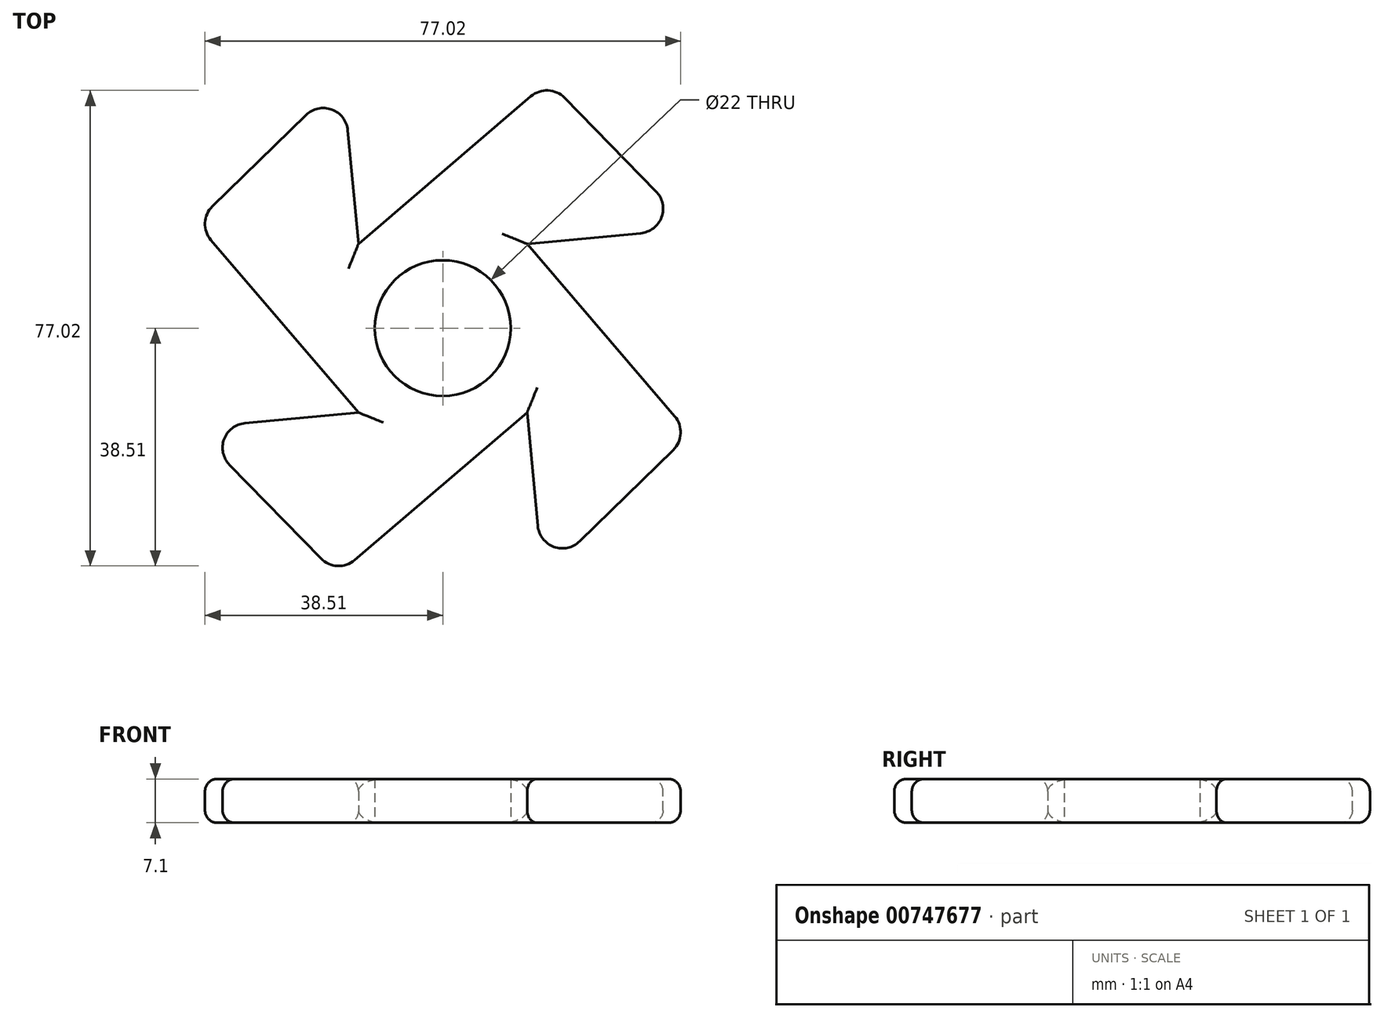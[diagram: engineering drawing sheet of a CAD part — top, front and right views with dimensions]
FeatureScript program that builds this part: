
annotation { "Feature Type Name" : "Feature", "Feature Type Description" : "" }
export const myFeature = defineFeature(function(context is Context, id is Id, definition is map)
    precondition{}
    {
        {
            var Q0;
            Q0=qCreatedBy(makeId("Top.planeOp"),FACE);
            var sketch = newSketch(context, id + "F0", { "sketchPlane" : qUnion([Q0])});
            skCircle(sketch, "E0", {"center": v(0, 0) * mm, "radius": 11 * mm});
            skCircle(sketch, "E1.cCircle", {"center": v(0, 0) * mm, "radius": 40.18 * mm, "construction": true});
            skLineSegment(sketch, "E1.0", {"start": v(39.98, -17.12) * mm, "end": v(16.17, -40.38) * mm});
            skLineSegment(sketch, "E1.1", {"start": v(16.17, -40.38) * mm, "end": v(-17.12, -39.98) * mm});
            skLineSegment(sketch, "E1.2", {"start": v(-17.12, -39.98) * mm, "end": v(-40.38, -16.17) * mm});
            skLineSegment(sketch, "E1.3", {"start": v(-40.38, -16.17) * mm, "end": v(-39.98, 17.12) * mm});
            skLineSegment(sketch, "E1.4", {"start": v(-39.98, 17.12) * mm, "end": v(-16.17, 40.38) * mm});
            skLineSegment(sketch, "E1.5", {"start": v(-16.17, 40.38) * mm, "end": v(17.12, 39.98) * mm});
            skLineSegment(sketch, "E1.6", {"start": v(17.12, 39.98) * mm, "end": v(40.38, 16.17) * mm});
            skLineSegment(sketch, "E1.7", {"start": v(40.38, 16.17) * mm, "end": v(39.98, -17.12) * mm});
            skPoint(sketch, "E1.0.midPoint", {"position": v(28.08, -28.75) * mm});
            skCircle(sketch, "E2.cCircle", {"center": v(0, 0) * mm, "radius": 13.65 * mm, "construction": true});
            skLineSegment(sketch, "E2.0", {"start": v(13.65, -13.65) * mm, "end": v(-13.65, -13.65) * mm});
            skLineSegment(sketch, "E2.1", {"start": v(-13.65, -13.65) * mm, "end": v(-13.65, 13.65) * mm});
            skLineSegment(sketch, "E2.2", {"start": v(-13.65, 13.65) * mm, "end": v(13.65, 13.65) * mm});
            skLineSegment(sketch, "E2.3", {"start": v(13.65, 13.65) * mm, "end": v(13.65, -13.65) * mm});
            skPoint(sketch, "E2.0.midPoint", {"position": v(0, -13.65) * mm});
            skLineSegment(sketch, "E3", {"start": v(-13.65, 13.65) * mm, "end": v(-16.17, 40.38) * mm});
            skLineSegment(sketch, "E4", {"start": v(-13.65, 13.65) * mm, "end": v(17.12, 39.98) * mm});
            skLineSegment(sketch, "E5", {"start": v(13.65, 13.65) * mm, "end": v(40.38, 16.17) * mm});
            skLineSegment(sketch, "E6", {"start": v(13.65, 13.65) * mm, "end": v(39.98, -17.12) * mm});
            skLineSegment(sketch, "E7", {"start": v(13.65, -13.65) * mm, "end": v(16.17, -40.38) * mm});
            skLineSegment(sketch, "E8", {"start": v(13.65, -13.65) * mm, "end": v(-17.12, -39.98) * mm});
            skLineSegment(sketch, "E9", {"start": v(-13.65, -13.65) * mm, "end": v(-40.38, -16.17) * mm});
            skLineSegment(sketch, "E10", {"start": v(-13.65, -13.65) * mm, "end": v(-39.98, 17.12) * mm});
            skSolve(sketch);
        }
        {
            var Q0;
            Q0=makeQuery(id+"F0.imprint","IMPRINT",FACE,{"disambiguationData":[TD([[makeQuery(id+"F0.imprint","IMPRINT",EDGE,{"derivedFrom":sQuery(id+"F0.wireOp",EDGE,"E0")}),-1.0]])]});
            var Q1;
            Q1=makeQuery(id+"F0.imprint","IMPRINT",FACE,{"disambiguationData":[TD([[makeQuery(id+"F0.imprint","IMPRINT",EDGE,{"derivedFrom":sQuery(id+"F0.wireOp",EDGE,"E1.6")}),-1.0]])]});
            var Q2;
            Q2=makeQuery(id+"F0.imprint","IMPRINT",FACE,{"disambiguationData":[TD([[makeQuery(id+"F0.imprint","IMPRINT",EDGE,{"derivedFrom":sQuery(id+"F0.wireOp",EDGE,"E1.0")}),-1.0]])]});
            var Q3;
            Q3=makeQuery(id+"F0.imprint","IMPRINT",FACE,{"disambiguationData":[TD([[makeQuery(id+"F0.imprint","IMPRINT",EDGE,{"derivedFrom":sQuery(id+"F0.wireOp",EDGE,"E1.2")}),-1.0]])]});
            var Q4;
            Q4=makeQuery(id+"F0.imprint","IMPRINT",FACE,{"disambiguationData":[TD([[makeQuery(id+"F0.imprint","IMPRINT",EDGE,{"derivedFrom":sQuery(id+"F0.wireOp",EDGE,"E1.4")}),-1.0]])]});
            extrude(context, id + "F1", {"entities" : qUnion([Q0, Q1, Q2, Q3, Q4]), "depth" : 7.1 * mm, "offsetDistance" : 25 * mm});
        }
        {
            var Q0;
            Q0=makeQuery(id+"F1.opExtrude","CAP_EDGE",EDGE,{"disambiguationData":[OSD([sQuery(id+"F0.wireOp",EDGE,"E8")])],"isStart":false});
            var Q1;
            Q1=makeQuery(id+"F1.opExtrude","CAP_EDGE",EDGE,{"disambiguationData":[OSD([sQuery(id+"F0.wireOp",EDGE,"E7")])],"isStart":false});
            var Q2;
            Q2=makeQuery(id+"F1.opExtrude","CAP_EDGE",EDGE,{"disambiguationData":[OSD([sQuery(id+"F0.wireOp",EDGE,"E1.0")])],"isStart":false});
            var Q3;
            Q3=makeQuery(id+"F1.opExtrude","CAP_EDGE",EDGE,{"disambiguationData":[OSD([sQuery(id+"F0.wireOp",EDGE,"E6")])],"isStart":false});
            var Q4;
            Q4=makeQuery(id+"F1.opExtrude","CAP_EDGE",EDGE,{"disambiguationData":[OSD([sQuery(id+"F0.wireOp",EDGE,"E5")])],"isStart":false});
            var Q5;
            Q5=makeQuery(id+"F1.opExtrude","CAP_EDGE",EDGE,{"disambiguationData":[OSD([sQuery(id+"F0.wireOp",EDGE,"E1.6")])],"isStart":false});
            var Q6;
            Q6=makeQuery(id+"F1.opExtrude","CAP_EDGE",EDGE,{"disambiguationData":[OSD([sQuery(id+"F0.wireOp",EDGE,"E4")])],"isStart":false});
            var Q7;
            Q7=makeQuery(id+"F1.opExtrude","CAP_EDGE",EDGE,{"disambiguationData":[OSD([sQuery(id+"F0.wireOp",EDGE,"E3")])],"isStart":false});
            var Q8;
            Q8=makeQuery(id+"F1.opExtrude","CAP_EDGE",EDGE,{"disambiguationData":[OSD([sQuery(id+"F0.wireOp",EDGE,"E1.4")])],"isStart":false});
            var Q9;
            Q9=makeQuery(id+"F1.opExtrude","CAP_EDGE",EDGE,{"disambiguationData":[OSD([sQuery(id+"F0.wireOp",EDGE,"E10")])],"isStart":false});
            var Q10;
            Q10=makeQuery(id+"F1.opExtrude","CAP_EDGE",EDGE,{"disambiguationData":[OSD([sQuery(id+"F0.wireOp",EDGE,"E9")])],"isStart":false});
            var Q11;
            Q11=makeQuery(id+"F1.opExtrude","CAP_EDGE",EDGE,{"disambiguationData":[OSD([sQuery(id+"F0.wireOp",EDGE,"E1.2")])],"isStart":false});
            var Q12;
            Q12=makeQuery(id+"F1.opExtrude","CAP_EDGE",EDGE,{"disambiguationData":[OSD([sQuery(id+"F0.wireOp",EDGE,"E1.2")])],"isStart":true});
            var Q13;
            Q13=makeQuery(id+"F1.opExtrude","CAP_EDGE",EDGE,{"disambiguationData":[OSD([sQuery(id+"F0.wireOp",EDGE,"E9")])],"isStart":true});
            var Q14;
            Q14=makeQuery(id+"F1.opExtrude","CAP_EDGE",EDGE,{"disambiguationData":[OSD([sQuery(id+"F0.wireOp",EDGE,"E10")])],"isStart":true});
            var Q15;
            Q15=makeQuery(id+"F1.opExtrude","CAP_EDGE",EDGE,{"disambiguationData":[OSD([sQuery(id+"F0.wireOp",EDGE,"E1.4")])],"isStart":true});
            var Q16;
            Q16=makeQuery(id+"F1.opExtrude","CAP_EDGE",EDGE,{"disambiguationData":[OSD([sQuery(id+"F0.wireOp",EDGE,"E3")])],"isStart":true});
            var Q17;
            Q17=makeQuery(id+"F1.opExtrude","CAP_EDGE",EDGE,{"disambiguationData":[OSD([sQuery(id+"F0.wireOp",EDGE,"E4")])],"isStart":true});
            var Q18;
            Q18=makeQuery(id+"F1.opExtrude","CAP_EDGE",EDGE,{"disambiguationData":[OSD([sQuery(id+"F0.wireOp",EDGE,"E1.6")])],"isStart":true});
            var Q19;
            Q19=makeQuery(id+"F1.opExtrude","CAP_EDGE",EDGE,{"disambiguationData":[OSD([sQuery(id+"F0.wireOp",EDGE,"E5")])],"isStart":true});
            var Q20;
            Q20=makeQuery(id+"F1.opExtrude","CAP_EDGE",EDGE,{"disambiguationData":[OSD([sQuery(id+"F0.wireOp",EDGE,"E6")])],"isStart":true});
            var Q21;
            Q21=makeQuery(id+"F1.opExtrude","CAP_EDGE",EDGE,{"disambiguationData":[OSD([sQuery(id+"F0.wireOp",EDGE,"E1.0")])],"isStart":true});
            var Q22;
            Q22=makeQuery(id+"F1.opExtrude","CAP_EDGE",EDGE,{"disambiguationData":[OSD([sQuery(id+"F0.wireOp",EDGE,"E7")])],"isStart":true});
            var Q23;
            Q23=makeQuery(id+"F1.opExtrude","CAP_EDGE",EDGE,{"disambiguationData":[OSD([sQuery(id+"F0.wireOp",EDGE,"E8")])],"isStart":true});
            fillet(context, id + "F2", {"entities" : qUnion([Q0, Q1, Q2, Q3, Q4, Q5, Q6, Q7, Q8, Q9, Q10, Q11, Q12, Q13, Q14, Q15, Q16, Q17, Q18, Q19, Q20, Q21, Q22, Q23]), "radius" : 2 * mm, "tangentPropagation" : true, "allowEdgeOverflow" : false});
        }
        {
            var Q0;
            Q0=makeQuery(id+"F1.opExtrude","SWEPT_EDGE",EDGE,{"disambiguationData":[OSD([sQuery(id+"F0.wireOp",EDGE,"E1.0"),sQuery(id+"F0.wireOp",EDGE,"E1.7"),sQuery(id+"F0.wireOp",EDGE,"E6")])]});
            var Q1;
            Q1=makeQuery(id+"F1.opExtrude","SWEPT_EDGE",EDGE,{"disambiguationData":[OSD([sQuery(id+"F0.wireOp",EDGE,"E1.5"),sQuery(id+"F0.wireOp",EDGE,"E1.6"),sQuery(id+"F0.wireOp",EDGE,"E4")])]});
            var Q2;
            Q2=makeQuery(id+"F1.opExtrude","SWEPT_EDGE",EDGE,{"disambiguationData":[OSD([sQuery(id+"F0.wireOp",EDGE,"E1.3"),sQuery(id+"F0.wireOp",EDGE,"E1.4"),sQuery(id+"F0.wireOp",EDGE,"E10")])]});
            var Q3;
            Q3=makeQuery(id+"F1.opExtrude","SWEPT_EDGE",EDGE,{"disambiguationData":[OSD([sQuery(id+"F0.wireOp",EDGE,"E1.1"),sQuery(id+"F0.wireOp",EDGE,"E1.2"),sQuery(id+"F0.wireOp",EDGE,"E8")])]});
            var Q4;
            Q4=makeQuery(id+"F1.opExtrude","SWEPT_EDGE",EDGE,{"disambiguationData":[OSD([sQuery(id+"F0.wireOp",EDGE,"E1.0"),sQuery(id+"F0.wireOp",EDGE,"E1.1"),sQuery(id+"F0.wireOp",EDGE,"E7")])]});
            var Q5;
            Q5=makeQuery(id+"F1.opExtrude","SWEPT_EDGE",EDGE,{"disambiguationData":[OSD([sQuery(id+"F0.wireOp",EDGE,"E1.2"),sQuery(id+"F0.wireOp",EDGE,"E1.3"),sQuery(id+"F0.wireOp",EDGE,"E9")])]});
            var Q6;
            Q6=makeQuery(id+"F1.opExtrude","SWEPT_EDGE",EDGE,{"disambiguationData":[OSD([sQuery(id+"F0.wireOp",EDGE,"E1.4"),sQuery(id+"F0.wireOp",EDGE,"E1.5"),sQuery(id+"F0.wireOp",EDGE,"E3")])]});
            var Q7;
            Q7=makeQuery(id+"F1.opExtrude","SWEPT_EDGE",EDGE,{"disambiguationData":[OSD([sQuery(id+"F0.wireOp",EDGE,"E1.6"),sQuery(id+"F0.wireOp",EDGE,"E1.7"),sQuery(id+"F0.wireOp",EDGE,"E5")])]});
            fillet(context, id + "F3", {"entities" : qUnion([Q0, Q1, Q2, Q3, Q4, Q5, Q6, Q7]), "radius" : 4 * mm, "tangentPropagation" : true, "allowEdgeOverflow" : false});
        }
    });
